# Revit family: NLRS_57_DUF_UN_verlopende-bocht-r=0_nijburg
name_source: partatom
category: Duct Fittings
units: mm (PartAtom-declared; Revit-internal decimal feet)

## family parameters
Always vertical = Yes
Cut with Voids When Loaded = No
Part Type = Elbow
Round Connector Dimension = Use Diameter
Shared = No
Work Plane-Based = No

## types (1)
- R=0
    Assembly Code = 57.70
    Default Elevation = 0 mm  [stored 0 ft]
    Description = Rechthoekige verlopende bocht met radius
    Manufacturer = Nijburg Products
    Model = Rechthoekige bocht met radius, verlopend
    NLRS_C_content_datum_gewijzigd = 16-05-2023
    NLRS_C_content_provider = Nijburg Klimaattechniek
    NLRS_C_content_versie = 1.20.02
    NLRS_C_description = Rechthoekige verlopende bocht met radius
    NLRS_C_model = Rechthoekige bocht met radius, verlopend
    NPR_Artikelcode = RHKV
    NPR_Radius = 0 mm  [stored 0 ft]
    Type Comments = Height in = Height out
    URL = https://nijburg-klimaattechniek.nl

note: [stored X ft] marks values corroborated as IEEE doubles in the binary element streams (Revit-internal decimal feet)

## geometry (parser evidence)
native form markers: Sweep x9
no freeform markers — native parametric forms only
